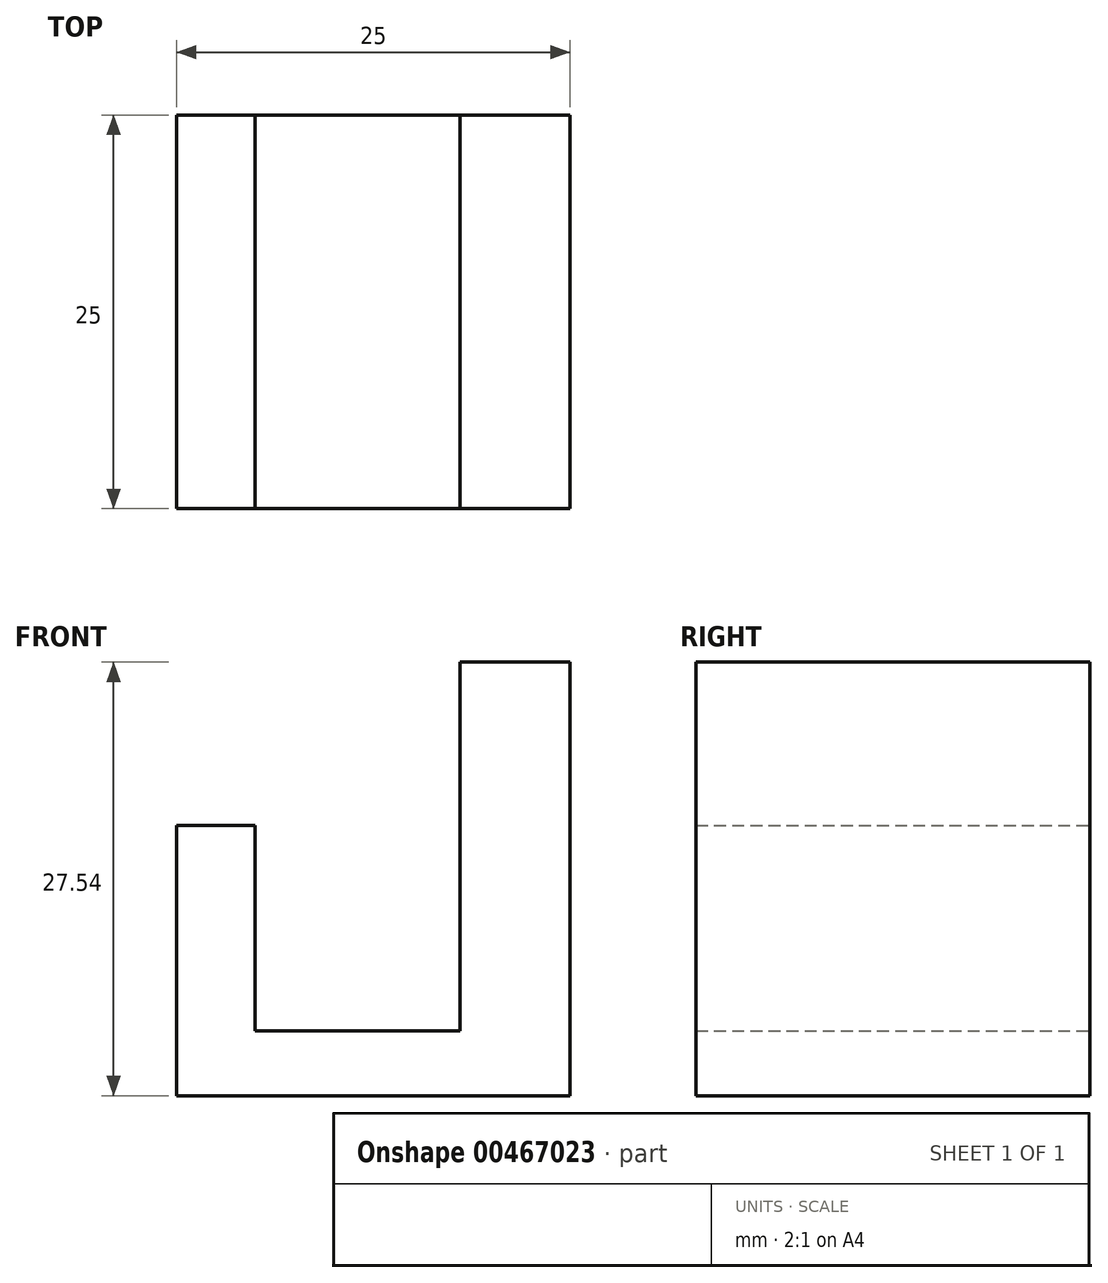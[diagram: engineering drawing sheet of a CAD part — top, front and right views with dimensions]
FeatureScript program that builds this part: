
annotation { "Feature Type Name" : "Feature", "Feature Type Description" : "" }
export const myFeature = defineFeature(function(context is Context, id is Id, definition is map)
    precondition{}
    {
        {
            var Q0;
            Q0=qCreatedBy(makeId("Front.planeOp"),FACE);
            var sketch = newSketch(context, id + "F0", { "sketchPlane" : qUnion([Q0])});
            skLineSegment(sketch, "E0", {"start": v(-7, 0) * mm, "end": v(-20, 0) * mm});
            skLineSegment(sketch, "E1", {"start": v(-20, 0) * mm, "end": v(-20, 13.04) * mm});
            skLineSegment(sketch, "E2", {"start": v(-20, 13.04) * mm, "end": v(-25, 13.04) * mm});
            skLineSegment(sketch, "E3", {"start": v(-25, 13.04) * mm, "end": v(-25, 0) * mm});
            skLineSegment(sketch, "E4", {"start": v(-25, 0) * mm, "end": v(-25, -4.12) * mm});
            skLineSegment(sketch, "E5", {"start": v(-25, -4.12) * mm, "end": v(0, -4.12) * mm});
            skLineSegment(sketch, "E6", {"start": v(0, -4.12) * mm, "end": v(0, 0) * mm});
            skLineSegment(sketch, "E7", {"start": v(0, 23.42) * mm, "end": v(-7, 23.42) * mm});
            skLineSegment(sketch, "E8", {"start": v(-7, 23.42) * mm, "end": v(-7, 0) * mm});
            skLineSegment(sketch, "E9", {"start": v(0, 23.42) * mm, "end": v(0, 0) * mm});
            skSolve(sketch);
        }
        {
            var Q0;
            Q0=makeQuery(id+"F0.imprint","IMPRINT",FACE,{"disambiguationData":[TD([[makeQuery(id+"F0.imprint","IMPRINT",EDGE,{"derivedFrom":sQuery(id+"F0.wireOp",EDGE,"E0")}),1.0]])]});
            extrude(context, id + "F1", {"entities" : qUnion([Q0]), "depth" : 25 * mm, "offsetDistance" : 25 * mm});
        }
    });
